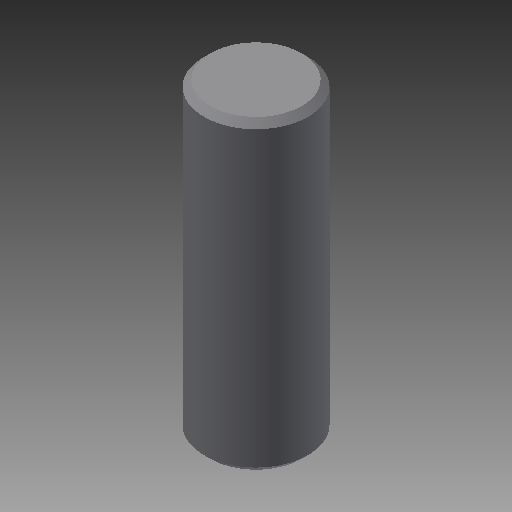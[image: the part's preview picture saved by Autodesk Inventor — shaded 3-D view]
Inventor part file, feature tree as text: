
AUTODESK INVENTOR PART (.ipt)
format: ipt  version: 2019.4 (Build 234330000, 330)  size: 146,944 bytes
history: native  units: in
note: dims shown in document units (in); Inventor stores cm internally (conversion verified against a paired STEP export)
features: other x112, revolve x1, sketch x1
ambient origin geometry x8: Origin, YZ Plane, XZ Plane, XY Plane, X Axis, Y Axis, Z Axis, Center Point
bodies: Solid1 (feature_tree)
feature tree (114):
  revolve  "Revolution1"  [1 undecoded]
  other  "b11_XY"
  other  "b11_YZ"
  other  "b11_ZX"
  other  "b11_X"
  other  "b11_Y"
  other  "b11_Z"
  other  "b11_Center"
  other  "b2_XY"
  other  "b2_YZ"
  other  "b2_ZX"
  other  "b2_X"
  other  "b2_Y"
  other  "b2_Z"
  other  "b2_Center"
  other  "f1_XY"
  other  "f1_YZ"
  other  "f1_ZX"
  other  "f1_X"
  other  "f1_Y"
  other  "f1_Z"
  other  "f1_Center"
  other  "f2_XY"
  other  "f2_YZ"
  other  "f2_ZX"
  other  "f2_X"
  other  "f2_Y"
  other  "f2_Z"
  other  "f2_Center"
  other  "h1_XY"
  other  "h1_YZ"
  other  "h1_ZX"
  other  "h1_X"
  other  "h1_Y"
  other  "h1_Z"
  other  "h1_Center"
  other  "h2_XY"
  other  "h2_YZ"
  other  "h2_ZX"
  other  "h2_X"
  other  "h2_Y"
  other  "h2_Z"
  other  "h2_Center"
  other  "npt1_XY"
  other  "npt1_YZ"
  other  "npt1_ZX"
  other  "npt1_X"
  other  "npt1_Y"
  other  "npt1_Z"
  other  "npt1_Center"
  other  "npt1_1_XY"
  other  "npt1_1_YZ"
  other  "npt1_1_ZX"
  other  "npt1_1_X"
  other  "npt1_1_Y"
  other  "npt1_1_Z"
  other  "npt1_1_Center"
  other  "npt2_XY"
  other  "npt2_YZ"
  other  "npt2_ZX"
  other  "npt2_X"
  other  "npt2_Y"
  other  "npt2_Z"
  other  "npt2_Center"
  other  "npt2_1_XY"
  other  "npt2_1_YZ"
  other  "npt2_1_ZX"
  other  "npt2_1_X"
  other  "npt2_1_Y"
  other  "npt2_1_Z"
  other  "npt2_1_Center"
  other  "rod_XY"
  other  "rod_YZ"
  other  "rod_ZX"
  other  "rod_X"
  other  "rod_Y"
  other  "rod_Z"
  other  "rod_Center"
  other  "rod_to_part_XY"
  other  "rod_to_part_YZ"
  other  "rod_to_part_ZX"
  other  "rod_to_part_X"
  other  "rod_to_part_Y"
  other  "rod_to_part_Z"
  other  "rod_to_part_Center"
  other  "th1_XY"
  other  "th1_YZ"
  other  "th1_ZX"
  other  "th1_X"
  other  "th1_Y"
  other  "th1_Z"
  other  "th1_Center"
  other  "th2_XY"
  other  "th2_YZ"
  other  "th2_ZX"
  other  "th2_X"
  other  "th2_Y"
  other  "th2_Z"
  other  "th2_Center"
  other  "to_rod_pivot_XY"
  other  "to_rod_pivot_YZ"
  other  "to_rod_pivot_ZX"
  other  "to_rod_pivot_X"
  other  "to_rod_pivot_Y"
  other  "to_rod_pivot_Z"
  other  "to_rod_pivot_Center"
  other  "to_rod_pivot1_XY"
  other  "to_rod_pivot1_YZ"
  other  "to_rod_pivot1_ZX"
  other  "to_rod_pivot1_X"
  other  "to_rod_pivot1_Y"
  other  "to_rod_pivot1_Z"
  other  "to_rod_pivot1_Center"
  sketch  "Sketch_10"  dims[d0=360.0deg d1=0.0in d2=0.0in d3=0.0in d4=0.0in d5=0.0in d6=0.0in d7=0.0in d8=0.0in d9=0.0in d10=0.0in d11=0.0in d12=0.0in d13=0.0in d14=0.0in]
note: 1 required parameter value undecoded (feature->parameter linkage not recoverable at this tier; creation-order binding heuristic only, values carry confidence <= 0.55)
